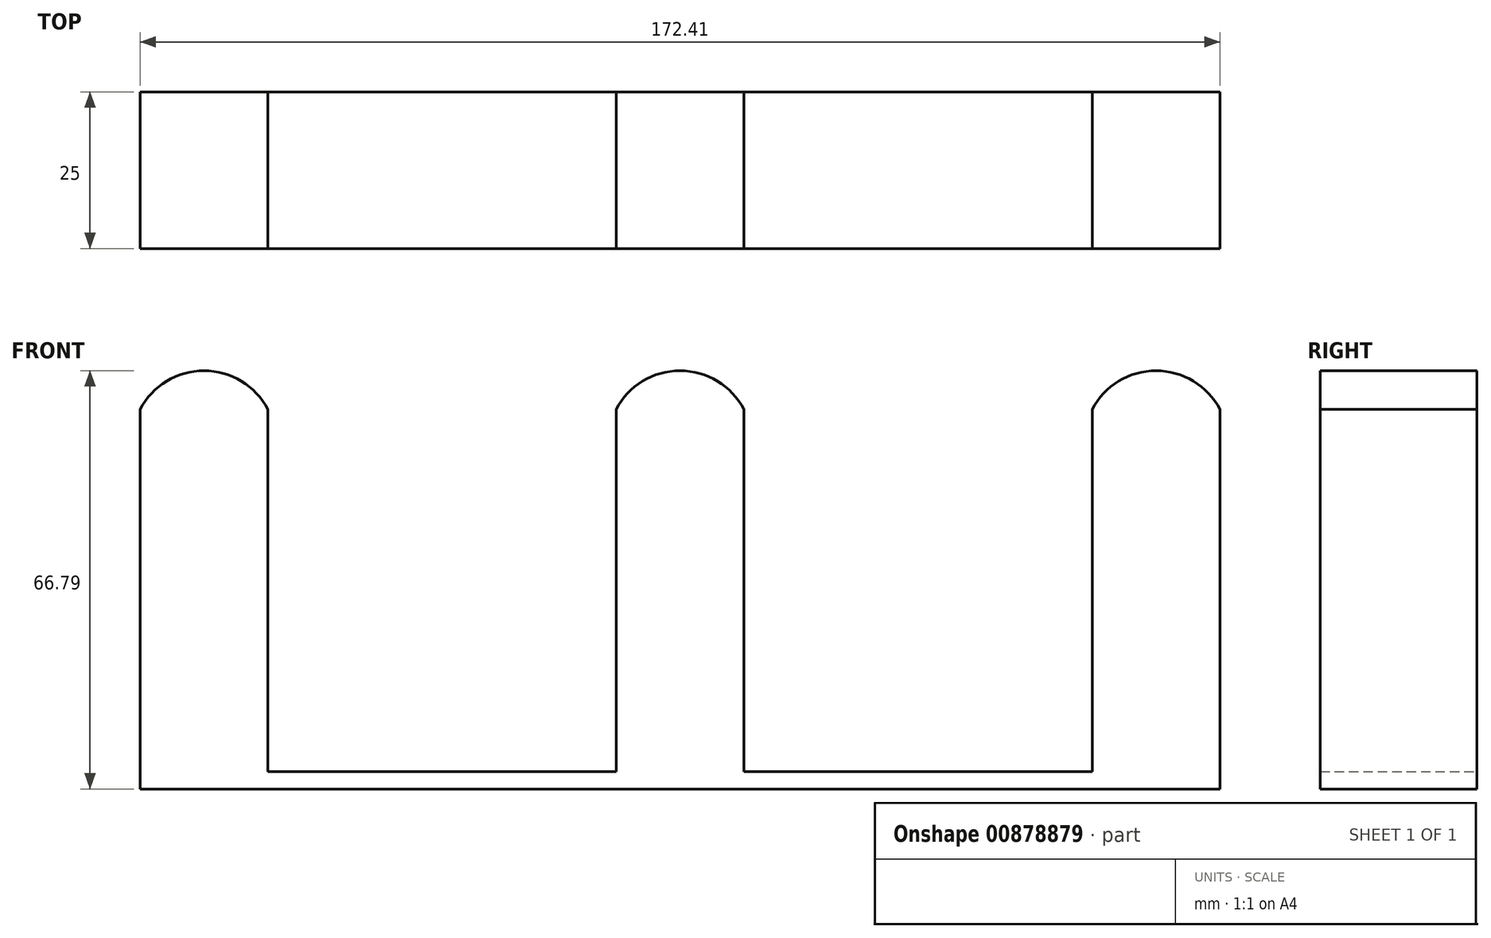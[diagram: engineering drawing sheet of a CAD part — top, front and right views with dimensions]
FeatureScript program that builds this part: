
annotation { "Feature Type Name" : "Feature", "Feature Type Description" : "" }
export const myFeature = defineFeature(function(context is Context, id is Id, definition is map)
    precondition{}
    {
        {
            var Q0;
            Q0=qCreatedBy(makeId("Front.planeOp"),FACE);
            var sketch = newSketch(context, id + "F0", { "sketchPlane" : qUnion([Q0])});
            skLineSegment(sketch, "E0", {"start": v(-86.74, 0) * mm, "end": v(111.16, 0) * mm});
            skLineSegment(sketch, "E1", {"start": v(-66.02, 64) * mm, "end": v(-66.02, -57.51) * mm, "construction": true});
            skLineSegment(sketch, "E2", {"start": v(-76.22, 0) * mm, "end": v(-76.22, 57.82) * mm});
            skLineSegment(sketch, "E3.MirrorCS", {"start": v(-55.81, 0) * mm, "end": v(-55.81, 57.82) * mm});
            skArc(sketch, "E4", {"start": v(-55.81, 57.82) * mm, "mid": v(-66.02, 64) * mm, "end": v(-76.22, 57.82) * mm});
            skLineSegment(sketch, "E5.1.0.0", {"start": v(-10.74, 0) * mm, "end": v(187.16, 0) * mm});
            skLineSegment(sketch, "E5.1.0.1", {"start": v(20.19, 0) * mm, "end": v(20.19, 57.82) * mm});
            skArc(sketch, "E5.1.0.2", {"start": v(20.19, 57.82) * mm, "mid": v(9.98, 64) * mm, "end": v(-0.22, 57.82) * mm});
            skLineSegment(sketch, "E5.1.0.3", {"start": v(-0.22, 0) * mm, "end": v(-0.22, 57.82) * mm});
            skLineSegment(sketch, "E5.1.0.4", {"start": v(9.98, 64) * mm, "end": v(9.98, -57.51) * mm, "construction": true});
            skLineSegment(sketch, "E5.2.0.0", {"start": v(65.26, 0) * mm, "end": v(263.16, 0) * mm});
            skLineSegment(sketch, "E5.2.0.1", {"start": v(96.19, 0) * mm, "end": v(96.19, 57.82) * mm});
            skArc(sketch, "E5.2.0.2", {"start": v(96.19, 57.82) * mm, "mid": v(85.98, 64) * mm, "end": v(75.78, 57.82) * mm});
            skLineSegment(sketch, "E5.2.0.3", {"start": v(75.78, 0) * mm, "end": v(75.78, 57.82) * mm});
            skLineSegment(sketch, "E5.2.0.4", {"start": v(85.98, 64) * mm, "end": v(85.98, -57.51) * mm, "construction": true});
            skLineSegment(sketch, "E5.direction1", {"start": v(-86.74, 0) * mm, "end": v(-10.74, 0) * mm, "construction": true});
            skLineSegment(sketch, "E6.bottom", {"start": v(-76.22, 0) * mm, "end": v(96.19, 0) * mm});
            skLineSegment(sketch, "E6.top", {"start": v(-76.22, -2.78) * mm, "end": v(96.19, -2.78) * mm});
            skLineSegment(sketch, "E6.left", {"start": v(-76.22, 0) * mm, "end": v(-76.22, -2.78) * mm});
            skLineSegment(sketch, "E6.right", {"start": v(96.19, 0) * mm, "end": v(96.19, -2.78) * mm});
            skSolve(sketch);
        }
        {
            var Q0;
            {var subQ0=sQuery(id+"F0.wireOp",EDGE,"E2");Q0=makeQuery(id+"F0.imprint","IMPRINT",FACE,{"disambiguationData":[TD([[makeQuery(id+"F0.imprint","IMPRINT",EDGE,{"derivedFrom":subQ0}),-1.0]])]});}
            var Q1;
            {var subQ0=sQuery(id+"F0.wireOp",EDGE,"E5.1.0.1");Q1=makeQuery(id+"F0.imprint","IMPRINT",FACE,{"disambiguationData":[TD([[makeQuery(id+"F0.imprint","IMPRINT",EDGE,{"derivedFrom":subQ0}),1.0]])]});}
            var Q2;
            {var subQ0=sQuery(id+"F0.wireOp",EDGE,"E5.2.0.1");Q2=makeQuery(id+"F0.imprint","IMPRINT",FACE,{"disambiguationData":[TD([[makeQuery(id+"F0.imprint","IMPRINT",EDGE,{"derivedFrom":subQ0}),1.0]])]});}
            var Q3;
            Q3=makeQuery(id+"F0.imprint","IMPRINT",FACE,{"disambiguationData":[TD([[makeQuery(id+"F0.imprint","IMPRINT",EDGE,{"derivedFrom":sQuery(id+"F0.wireOp",EDGE,"E6.top")}),1.0]])]});
            extrude(context, id + "F1", {"entities" : qUnion([Q0, Q1, Q2, Q3]), "depth" : 25 * mm, "offsetDistance" : 25 * mm});
        }
    });
